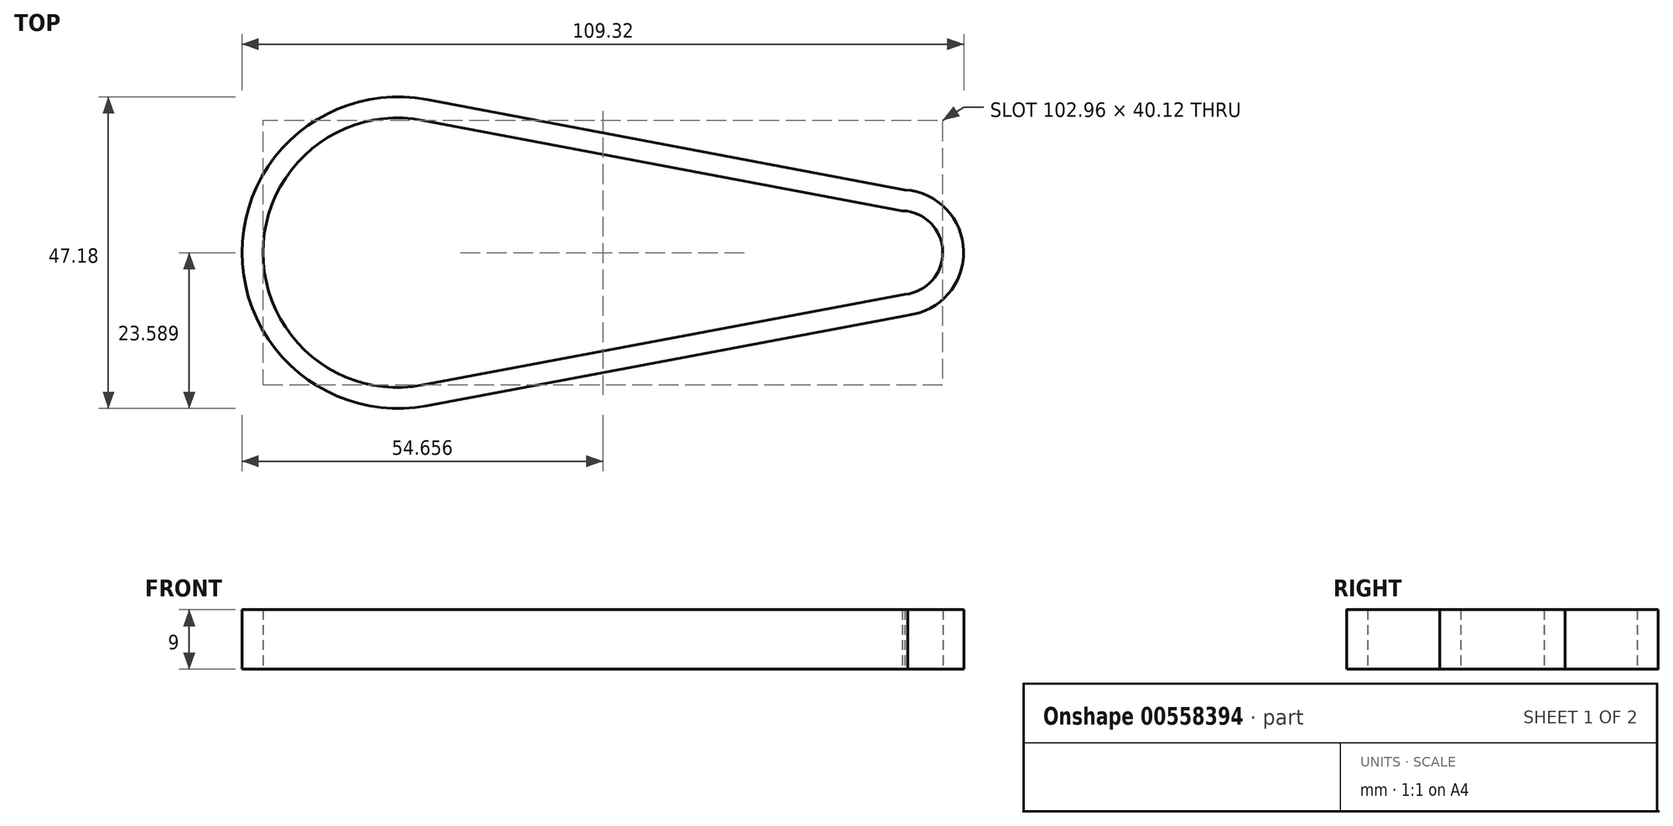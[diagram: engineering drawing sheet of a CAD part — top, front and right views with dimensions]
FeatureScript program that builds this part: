
annotation { "Feature Type Name" : "Feature", "Feature Type Description" : "" }
export const myFeature = defineFeature(function(context is Context, id is Id, definition is map)
    precondition{}
    {
        {
            var Q0;
            Q0=qCreatedBy(makeId("Top.planeOp"),FACE);
            var sketch = newSketch(context, id + "F0", { "sketchPlane" : qUnion([Q0])});
            skArc(sketch, "E0", {"start": v(3.79, 20.06) * mm, "mid": v(-20.42, 0) * mm, "end": v(3.78, -20.06) * mm});
            skLineSegment(sketch, "E1", {"start": v(0, 0) * mm, "end": v(76.2, 0) * mm, "construction": true});
            skArc(sketch, "E2", {"start": v(76.8, -6.32) * mm, "mid": v(82.55, 0.18) * mm, "end": v(76.44, 6.35) * mm});
            skLineSegment(sketch, "E3", {"start": v(76.44, 6.35) * mm, "end": v(3.79, 20.06) * mm});
            skLineSegment(sketch, "E4", {"start": v(76.8, -6.32) * mm, "end": v(3.78, -20.06) * mm});
            skLineSegment(sketch, "E5.0", {"start": v(76.82, 9.5) * mm, "end": v(4.38, 23.18) * mm});
            skArc(sketch, "E5.1", {"start": v(77.25, -9.47) * mm, "mid": v(85.72, 0.22) * mm, "end": v(76.82, 9.5) * mm});
            skLineSegment(sketch, "E5.2", {"start": v(77.25, -9.47) * mm, "end": v(4.36, -23.18) * mm});
            skArc(sketch, "E5.3", {"start": v(4.38, 23.18) * mm, "mid": v(-23.6, 0) * mm, "end": v(4.36, -23.18) * mm});
            skSolve(sketch);
        }
        {
            var Q0;
            Q0=makeQuery(id+"F0.imprint","IMPRINT",FACE,{"disambiguationData":[TD([[makeQuery(id+"F0.imprint","IMPRINT",EDGE,{"derivedFrom":sQuery(id+"F0.wireOp",EDGE,"E0")}),-1.0]])]});
            extrude(context, id + "F1", {"entities" : qUnion([Q0]), "depth" : 9 * mm, "offsetDistance" : 25.4 * mm});
        }
    });
